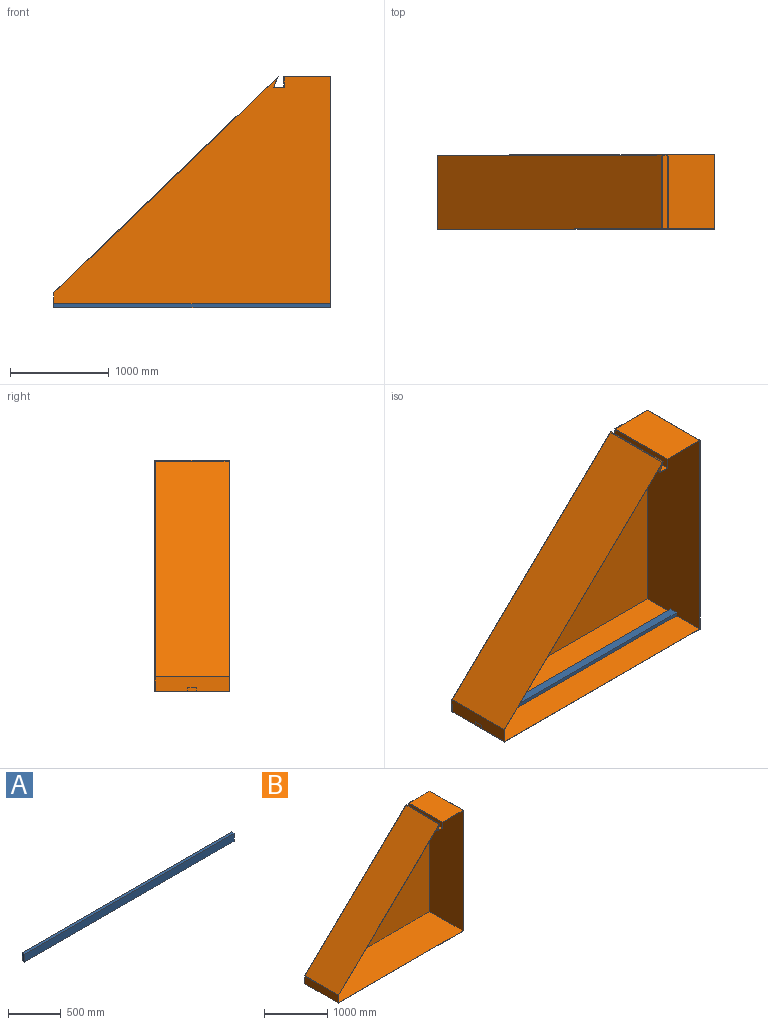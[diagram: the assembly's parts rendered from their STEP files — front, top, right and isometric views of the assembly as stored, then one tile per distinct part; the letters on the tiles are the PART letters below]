
ASSEMBLY  parts=2 mates=1
PART A: 6 faces, bbox 2800x38x89 mm
  f0: plane 2800x38mm, normal (0,0,-1), area 106400mm2, adj f1,f3,f4,f5
  f1: plane 89x38mm, normal (1,0,0), area 3382mm2, adj f0,f2,f4,f5
  f2: plane 2800x38mm, normal (0,0,1), area 106400mm2, adj f1,f3,f4,f5
  f3: plane 89x38mm, normal (-1,0,0), area 3382mm2, adj f0,f2,f4,f5
  f4: plane 2800x89mm, normal (0,-1,0), area 249200mm2, adj f0,f1,f2,f3
  f5: plane 2800x89mm, normal (0,1,0), area 249200mm2, adj f0,f1,f2,f3
PART B: 19 faces, bbox 2800x750x2340 mm
  f0: plane 2800x2340mm, normal (0,-1,0), area 23066.1mm2, adj f1,f2,f3,f4,f5,f6,f7,f8
  f1: plane 2800x750mm, normal (0,0,-1), area 2100000mm2, adj f0,f2,f8,f9
  f2: plane 2340x750mm, normal (1,0,0), area 1755000mm2, adj f0,f1,f3,f9
  f3: plane 750x470mm, normal (0,0,1), area 352500mm2, adj f0,f2,f4,f9
  f4: plane 750x110mm, normal (-1,0,0), area 82500mm2, adj f0,f3,f5,f9
  f5: plane 750x100mm, normal (0,0,1), area 75000mm2, adj f0,f4,f6,f9
  f6: plane 750x110mm, normal (0.94,0,-0.35), area 88072.3mm2, adj f0,f5,f7,f9
  f7: plane 2271.11x2190mm, normal (-0.69,0,0.72), area 2366250mm2, adj f0,f6,f8,f9
  f8: plane 750x150mm, normal (-1,0,0), area 112500mm2, adj f0,f1,f7,f9
  f9: plane 2800x2340mm, normal (0,1,0), area 4056399.2mm2, adj f1,f2,f3,f4,f5,f6,f7,f8
  f10: plane 2795x747.5mm, normal (0,0,1), area 2089262.5mm2, adj f0,f11,f17,f18
  f11: plane 2335x747.5mm, normal (-1,0,0), area 1745412.5mm2, adj f0,f10,f12,f18
  f12: plane 747.5x465mm, normal (0,0,-1), area 347587.5mm2, adj f0,f11,f13,f18
  f13: plane 747.5x110mm, normal (1,0,0), area 82225mm2, adj f0,f12,f14,f18
  f14: plane 747.5x106.1mm, normal (0,0,-1), area 79312.1mm2, adj f0,f13,f15,f18
  f15: plane 747.5x103.05mm, normal (-0.94,0,0.35), area 82230.4mm2, adj f0,f14,f16,f18
  f16: plane 2262.41x2181.61mm, normal (0.69,0,-0.72), area 2349326.8mm2, adj f0,f15,f17,f18
  f17: plane 747.5x146.44mm, normal (1,0,0), area 109462.2mm2, adj f0,f10,f16,f18
  f18: plane 2795x2335mm, normal (0,-1,0), area 4033333.1mm2, adj f10,f11,f12,f13,f14,f15,f16,f17
PLACE A rot(axis=(1,0,0),90deg) t=(217.22,-758.16,-136.95)mm
PLACE B at identity
MATE fastened A.f4 <-> B.f10  axis (0,0,-1) through (1334.88,-376.25,-177.45)mm
